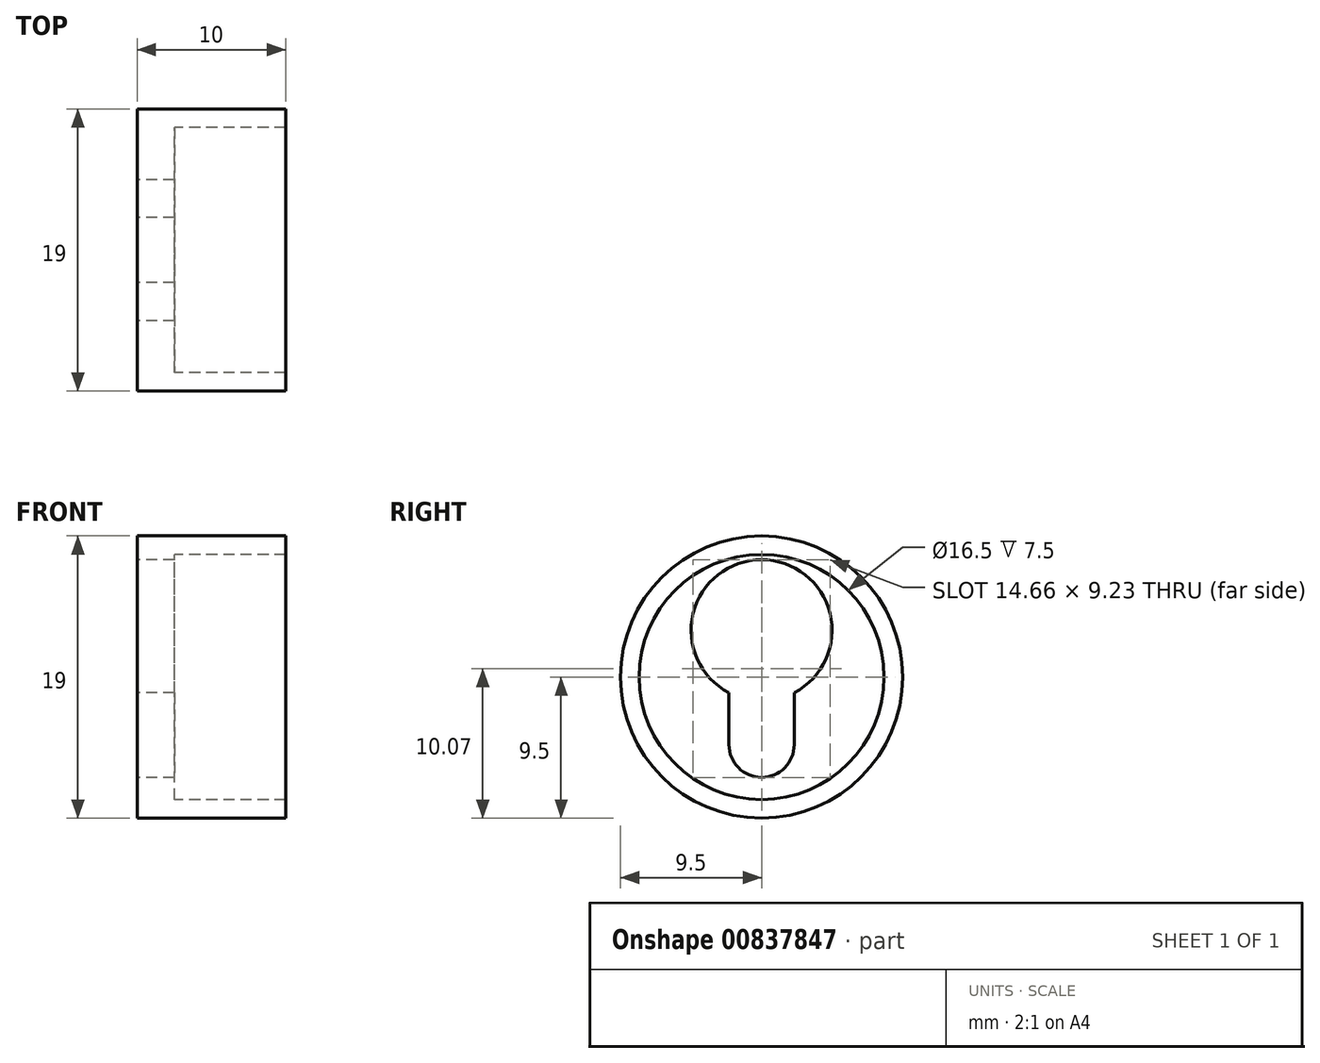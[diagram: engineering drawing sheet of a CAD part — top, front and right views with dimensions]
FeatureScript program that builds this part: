
annotation { "Feature Type Name" : "Feature", "Feature Type Description" : "" }
export const myFeature = defineFeature(function(context is Context, id is Id, definition is map)
    precondition{}
    {
        {
            var Q0;
            Q0=qCreatedBy(makeId("Right.planeOp"),FACE);
            var sketch = newSketch(context, id + "F0", { "sketchPlane" : qUnion([Q0])});
            skCircle(sketch, "E0", {"center": v(0, 0) * mm, "radius": 9.5 * mm});
            skCircle(sketch, "E1", {"center": v(0, 3.15) * mm, "radius": 4.75 * mm});
            skLineSegment(sketch, "E2", {"start": v(-2.2, -1.06) * mm, "end": v(-2.2, -4.56) * mm});
            skLineSegment(sketch, "E3", {"start": v(2.2, -1.06) * mm, "end": v(2.2, -4.56) * mm});
            skArc(sketch, "E4", {"start": v(-2.2, -4.56) * mm, "mid": v(0, -6.76) * mm, "end": v(2.2, -4.56) * mm});
            skCircle(sketch, "E5", {"center": v(0, 0) * mm, "radius": 8.25 * mm});
            skSolve(sketch);
        }
        {
            var Q0;
            Q0=makeQuery(id+"F0.imprint","IMPRINT",FACE,{"disambiguationData":[TD([[makeQuery(id+"F0.imprint","IMPRINT",EDGE,{"derivedFrom":sQuery(id+"F0.wireOp",EDGE,"E0")}),1.0]])]});
            var Q1;
            {var subQ1=sQuery(id+"F0.wireOp",EDGE,"E2");Q1=makeQuery(id+"F0.imprint","IMPRINT",FACE,{"disambiguationData":[TD([[makeQuery(id+"F0.imprint","IMPRINT",EDGE,{"derivedFrom":subQ1}),-1.0]])]});}
            extrude(context, id + "F1", {"entities" : qUnion([Q0, Q1]), "depth" : 2.5 * mm, "offsetDistance" : 25 * mm});
        }
        {
            var Q0;
            Q0=makeQuery(id+"F0.imprint","IMPRINT",FACE,{"disambiguationData":[TD([[makeQuery(id+"F0.imprint","IMPRINT",EDGE,{"derivedFrom":sQuery(id+"F0.wireOp",EDGE,"E0")}),1.0]])]});
            extrude(context, id + "F2", {"entities" : qUnion([Q0]), "operationType" : NewBodyOperationType.ADD, "depth" : 10 * mm, "offsetDistance" : 25 * mm});
        }
    });
